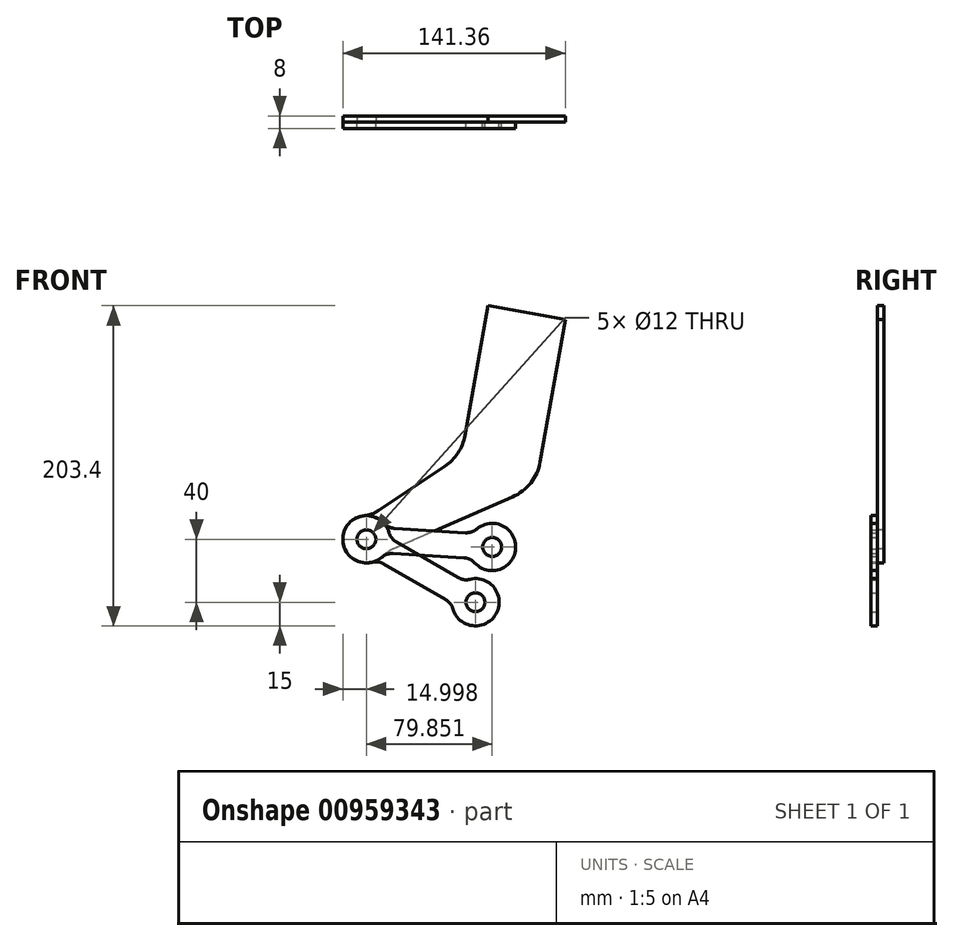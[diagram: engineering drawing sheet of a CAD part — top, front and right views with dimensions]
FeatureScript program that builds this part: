
annotation { "Feature Type Name" : "Feature", "Feature Type Description" : "" }
export const myFeature = defineFeature(function(context is Context, id is Id, definition is map)
    precondition{}
    {
        {
            var Q0;
            Q0=qCreatedBy(makeId("Front.planeOp"),FACE);
            var sketch = newSketch(context, id + "F0", { "sketchPlane" : qUnion([Q0])});
            skCircle(sketch, "E0", {"center": v(0, 0) * mm, "radius": 100 * mm, "construction": true});
            skLineSegment(sketch, "E1", {"start": v(0, 0) * mm, "end": v(82.88, 470.03) * mm});
            skLineSegment(sketch, "E2", {"start": v(0, 0) * mm, "end": v(-69.28, 40) * mm});
            skLineSegment(sketch, "E3", {"start": v(-243.07, -98.8) * mm, "end": v(407.08, -102.02) * mm});
            skArc(sketch, "E4", {"start": v(0, 0) * mm, "mid": v(7.3, 16.89) * mm, "end": v(10.56, 35) * mm, "construction": true});
            skCircle(sketch, "E5", {"center": v(10.56, 35) * mm, "radius": 100 * mm, "construction": true});
            skLineSegment(sketch, "E6", {"start": v(10.56, 35) * mm, "end": v(-69.28, 40) * mm, "construction": true});
            skArc(sketch, "E7", {"start": v(-54.87, 44.15) * mm, "mid": v(-82.27, 47.5) * mm, "end": v(-65.67, 25.44) * mm});
            skArc(sketch, "E8", {"start": v(-14.41, -4.15) * mm, "mid": v(13, -7.5) * mm, "end": v(-3.61, 14.56) * mm});
            skLineSegment(sketch, "E9", {"start": v(-50.26, 38.25) * mm, "end": v(-11.02, 15.6) * mm});
            skLineSegment(sketch, "E10.MirrorCS", {"start": v(-58.26, 24.4) * mm, "end": v(-19.02, 1.75) * mm});
            skPoint(sketch, "E11.visualSharp", {"position": v(-54.3, 40.58) * mm});
            skArc(sketch, "E11.filletArc", {"start": v(-54.87, 44.15) * mm, "mid": v(-53.13, 40.75) * mm, "end": v(-50.26, 38.25) * mm});
            skPoint(sketch, "E12.visualSharp", {"position": v(-62.3, 26.73) * mm});
            skArc(sketch, "E12.filletArc", {"start": v(-58.26, 24.4) * mm, "mid": v(-61.86, 25.64) * mm, "end": v(-65.67, 25.44) * mm});
            skPoint(sketch, "E13.visualSharp", {"position": v(-14.99, -0.58) * mm});
            skArc(sketch, "E13.filletArc", {"start": v(-14.41, -4.15) * mm, "mid": v(-16.15, -0.75) * mm, "end": v(-19.02, 1.75) * mm});
            skPoint(sketch, "E14.visualSharp", {"position": v(-6.99, 13.27) * mm});
            skArc(sketch, "E14.filletArc", {"start": v(-11.02, 15.6) * mm, "mid": v(-7.42, 14.36) * mm, "end": v(-3.61, 14.56) * mm});
            skCircle(sketch, "E15", {"center": v(-69.28, 40) * mm, "radius": 6 * mm});
            skCircle(sketch, "E16", {"center": v(0, 0) * mm, "radius": 6 * mm});
            skSolve(sketch);
        }
        {
            var Q0;
            Q0=qCreatedBy(makeId("Front.planeOp"),FACE);
            var sketch = newSketch(context, id + "F1", { "sketchPlane" : qUnion([Q0])});
            skCircle(sketch, "E17.0", {"center": v(0, 0) * mm, "radius": 100 * mm, "construction": true});
            skArc(sketch, "E18.converted", {"start": v(-70.74, 54.93) * mm, "mid": v(-82.8, 33.5) * mm, "end": v(-58.54, 29.53) * mm});
            skPoint(sketch, "E19.orphan", {"position": v(-54.87, 44.15) * mm});
            skLineSegment(sketch, "E20", {"start": v(-69.28, 40) * mm, "end": v(131.28, 40) * mm, "construction": true});
            skLineSegment(sketch, "E21", {"start": v(41.11, 89.18) * mm, "end": v(57.08, 179.72) * mm});
            skLineSegment(sketch, "E22", {"start": v(7.83, 188.4) * mm, "end": v(57.08, 179.72) * mm});
            skLineSegment(sketch, "E23", {"start": v(23.54, 66.89) * mm, "end": v(-52.2, 33.92) * mm});
            skLineSegment(sketch, "E24", {"start": v(-61.57, 58.2) * mm, "end": v(-19.59, 86.22) * mm});
            skLineSegment(sketch, "E25.trimOffspring", {"start": v(-6.7, 105.97) * mm, "end": v(7.83, 188.4) * mm});
            skPoint(sketch, "E26.MirrorCS.start.orphan", {"position": v(-18.21, 40.68) * mm});
            skPoint(sketch, "E27.visualSharp", {"position": v(-8.93, 93.34) * mm});
            skArc(sketch, "E27.filletArc", {"start": v(-19.59, 86.22) * mm, "mid": v(-11.12, 94.78) * mm, "end": v(-6.7, 105.97) * mm});
            skPoint(sketch, "E28.visualSharp", {"position": v(38.31, 73.32) * mm});
            skArc(sketch, "E28.filletArc", {"start": v(23.54, 66.89) * mm, "mid": v(35.13, 75.83) * mm, "end": v(41.11, 89.18) * mm});
            skArc(sketch, "E29.trimOffspring", {"start": v(-54.28, 40) * mm, "mid": v(-54.43, 42.1) * mm, "end": v(-54.87, 44.15) * mm});
            skPoint(sketch, "E30.visualSharp", {"position": v(-66.7, 54.78) * mm});
            skArc(sketch, "E30.filletArc", {"start": v(-70.74, 54.93) * mm, "mid": v(-65.95, 56) * mm, "end": v(-61.57, 58.2) * mm});
            skPoint(sketch, "E31.visualSharp", {"position": v(-56.6, 32) * mm});
            skArc(sketch, "E31.filletArc", {"start": v(-52.2, 33.92) * mm, "mid": v(-55.58, 32.03) * mm, "end": v(-58.54, 29.53) * mm});
            skCircle(sketch, "E32", {"center": v(-69.28, 40) * mm, "radius": 6 * mm});
            skSolve(sketch);
        }
        {
            var Q0;
            Q0=makeQuery(id+"F0.imprint","IMPRINT",FACE,{"disambiguationData":[TD([[makeQuery(id+"F0.imprint","IMPRINT",EDGE,{"derivedFrom":sQuery(id+"F0.wireOp",EDGE,"E7")}),1.0]])]});
            extrude(context, id + "F2", {"entities" : qUnion([Q0]), "depth" : 4 * mm, "offsetDistance" : 25 * mm});
        }
        {
            var Q0;
            Q0=makeQuery(id+"F1.imprint","IMPRINT",FACE,{"disambiguationData":[TD([[makeQuery(id+"F1.imprint","IMPRINT",EDGE,{"derivedFrom":sQuery(id+"F1.wireOp",EDGE,"E18.converted")}),1.0]])]});
            var Q1;
            {var subQ4=sQuery(id+"F1.wireOp",EDGE,"E22");Q1=makeQuery(id+"F1.imprint","IMPRINT",FACE,{"disambiguationData":[TD([[makeQuery(id+"F1.imprint","IMPRINT",EDGE,{"derivedFrom":subQ4}),-1.0]])]});}
            extrude(context, id + "F3", {"entities" : qUnion([Q0, Q1]), "oppositeDirection" : true, "depth" : 4 * mm, "offsetDistance" : 25 * mm});
        }
        {
            var Q0;
            Q0=sQuery(id+"F0.wireOp",VERTEX,"E2.end");
            var Q1;
            Q1=sQuery(id+"F1.wireOp",EDGE,"E32");
            cPlane(context, id + "F4", {"entities" : qUnion([Q0, Q1]), "cplaneType" : CPlaneType.CURVE_POINT, "offset" : 25 * mm, "width" : 150 * mm, "height" : 150 * mm});
        }
        {
            var Q0;
            Q0=qCreatedBy(id+"F4.planeOp",FACE);
            var sketch = newSketch(context, id + "F5", { "sketchPlane" : qUnion([Q0])});
            skPoint(sketch, "E33.0", {"position": v(-69.28, 0) * mm});
            skLineSegment(sketch, "E34", {"start": v(-69.28, 0) * mm, "end": v(-69.28, 43.35) * mm, "construction": true});
            skSolve(sketch);
        }
        {
            var Q0;
            Q0=makeQuery(id+"F2.opExtrude","SWEPT_BODY",BODY,{"disambiguationData":[OSD([sQuery(id+"F0.wireOp",EDGE,"E7"),sQuery(id+"F0.wireOp",EDGE,"E8"),sQuery(id+"F0.wireOp",EDGE,"E9"),sQuery(id+"F0.wireOp",EDGE,"E10.MirrorCS"),sQuery(id+"F0.wireOp",EDGE,"E11.filletArc"),sQuery(id+"F0.wireOp",EDGE,"E12.filletArc"),sQuery(id+"F0.wireOp",EDGE,"E13.filletArc"),sQuery(id+"F0.wireOp",EDGE,"E14.filletArc"),sQuery(id+"F0.wireOp",EDGE,"E15"),sQuery(id+"F0.wireOp",EDGE,"E16")])]});
            var Q1;
            Q1=sQuery(id+"F5.wireOp",EDGE,"E34");
            transform(context, id + "F6", {"entities" : qUnion([Q0]), "transformType" : TransformType.ROTATION, "transformAxis" : qUnion([Q1]), "angle" : 26.5 * degree, "makeCopy" : true});
        }
    });
